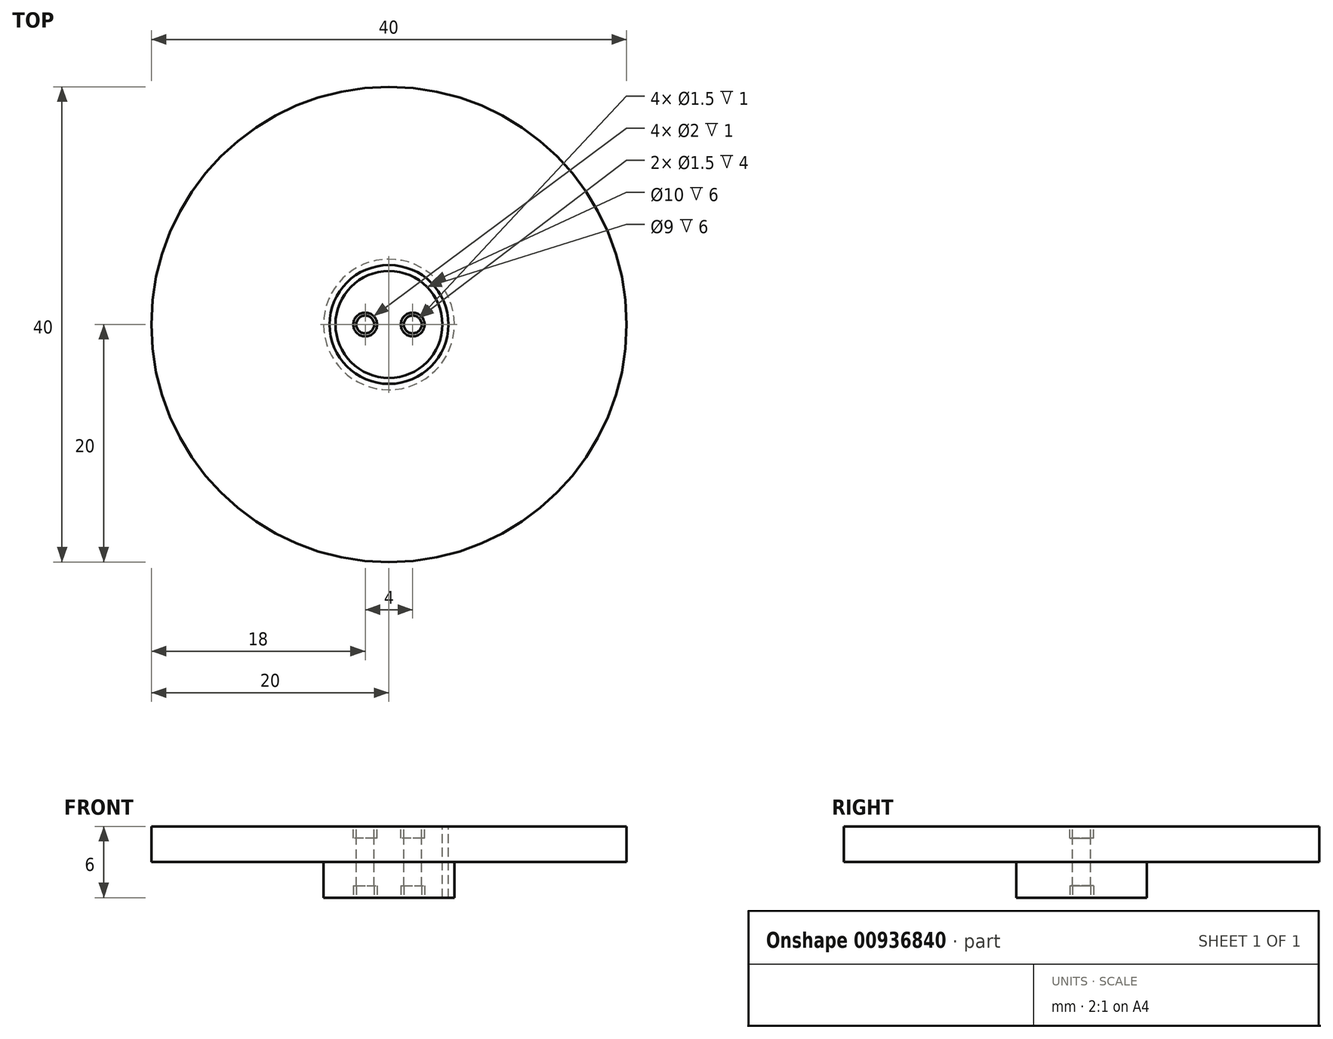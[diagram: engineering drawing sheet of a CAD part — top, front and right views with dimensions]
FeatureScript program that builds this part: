
annotation { "Feature Type Name" : "Feature", "Feature Type Description" : "" }
export const myFeature = defineFeature(function(context is Context, id is Id, definition is map)
    precondition{}
    {
        {
            var Q0;
            Q0=qCreatedBy(makeId("Top.planeOp"),FACE);
            var sketch = newSketch(context, id + "F0", { "sketchPlane" : qUnion([Q0])});
            skCircle(sketch, "E0", {"center": v(0, 0) * mm, "radius": 20 * mm});
            skCircle(sketch, "E1", {"center": v(0, 0) * mm, "radius": 5.5 * mm});
            skSolve(sketch);
        }
        {
            var Q0;
            Q0=makeQuery(id+"F0.imprint","IMPRINT",FACE,{"disambiguationData":[TD([[makeQuery(id+"F0.imprint","IMPRINT",EDGE,{"derivedFrom":sQuery(id+"F0.wireOp",EDGE,"E0")}),1.0]])]});
            extrude(context, id + "F1", {"entities" : qUnion([Q0]), "depth" : 3 * mm, "offsetDistance" : 25 * mm});
        }
        {
            var Q0;
            Q0=makeQuery(id+"F1.opExtrude","CAP_FACE",FACE,{"disambiguationData":[OSD([sQuery(id+"F0.wireOp",EDGE,"E0"),sQuery(id+"F0.wireOp",EDGE,"E1")])],"isStart":false});
            var sketch = newSketch(context, id + "F2", { "sketchPlane" : qUnion([Q0])});
            skCircle(sketch, "E2", {"center": v(0, 0) * mm, "radius": 5.5 * mm});
            skCircle(sketch, "E3", {"center": v(0, 0) * mm, "radius": 5 * mm});
            skSolve(sketch);
        }
        {
            var Q0;
            Q0 = qSketchRegion(id + "F2", true);
            extrude(context, id + "F3", {"entities" : qUnion([Q0]), "operationType" : NewBodyOperationType.ADD, "oppositeDirection" : true, "depth" : 6 * mm, "offsetDistance" : 25 * mm});
        }
        {
            var Q0;
            Q0=makeQuery(id+"F3.boolean.opBoolean","MERGE",FACE,{"derivedFrom":[makeQuery(id+"F1.opExtrude","CAP_FACE",FACE,{"disambiguationData":[OSD([sQuery(id+"F0.wireOp",EDGE,"E0"),sQuery(id+"F0.wireOp",EDGE,"E1")])],"isStart":false}),makeQuery(id+"F3.opExtrude","CAP_FACE",FACE,{"disambiguationData":[OSD([sQuery(id+"F2.wireOp",EDGE,"E2"),sQuery(id+"F2.wireOp",EDGE,"E3")])],"isStart":true})]});
            var sketch = newSketch(context, id + "F4", { "sketchPlane" : qUnion([Q0])});
            skCircle(sketch, "E4", {"center": v(0, 0) * mm, "radius": 5 * mm});
            skCircle(sketch, "E5", {"center": v(0, 0) * mm, "radius": 4.5 * mm});
            skSolve(sketch);
        }
        {
            var Q0;
            Q0 = qSketchRegion(id + "F4", true);
            extrude(context, id + "F5", {"entities" : qUnion([Q0]), "oppositeDirection" : true, "depth" : 6 * mm, "offsetDistance" : 25 * mm});
        }
        {
            var Q0;
            Q0=makeQuery(id+"F3.boolean.opBoolean","MERGE",FACE,{"derivedFrom":[makeQuery(id+"F1.opExtrude","CAP_FACE",FACE,{"disambiguationData":[OSD([sQuery(id+"F0.wireOp",EDGE,"E0"),sQuery(id+"F0.wireOp",EDGE,"E1")])],"isStart":false}),makeQuery(id+"F3.opExtrude","CAP_FACE",FACE,{"disambiguationData":[OSD([sQuery(id+"F2.wireOp",EDGE,"E2"),sQuery(id+"F2.wireOp",EDGE,"E3")])],"isStart":true})]});
            var sketch = newSketch(context, id + "F6", { "sketchPlane" : qUnion([Q0])});
            skCircle(sketch, "E6", {"center": v(0, 0) * mm, "radius": 4.5 * mm});
            skSolve(sketch);
        }
        {
            var Q0;
            Q0 = qSketchRegion(id + "F6", true);
            extrude(context, id + "F7", {"entities" : qUnion([Q0]), "oppositeDirection" : true, "depth" : 6 * mm, "offsetDistance" : 25 * mm});
        }
        {
            var Q0;
            Q0=makeQuery(id+"F3.boolean.opBoolean","MERGE",FACE,{"derivedFrom":[makeQuery(id+"F1.opExtrude","CAP_FACE",FACE,{"disambiguationData":[OSD([sQuery(id+"F0.wireOp",EDGE,"E0"),sQuery(id+"F0.wireOp",EDGE,"E1")])],"isStart":false}),makeQuery(id+"F3.opExtrude","CAP_FACE",FACE,{"disambiguationData":[OSD([sQuery(id+"F2.wireOp",EDGE,"E2"),sQuery(id+"F2.wireOp",EDGE,"E3")])],"isStart":true})]});
            var sketch = newSketch(context, id + "F8", { "sketchPlane" : qUnion([Q0])});
            skCircle(sketch, "E7", {"center": v(-2, 0) * mm, "radius": 1 * mm});
            skCircle(sketch, "E8", {"center": v(2, 0) * mm, "radius": 1 * mm});
            skSolve(sketch);
        }
        {
            var Q0;
            Q0 = qSketchRegion(id + "F8", true);
            extrude(context, id + "F9", {"entities" : qUnion([Q0]), "operationType" : NewBodyOperationType.REMOVE, "oppositeDirection" : true, "depth" : 1 * mm, "offsetDistance" : 25 * mm});
        }
        {
            var Q0;
            Q0=makeQuery(id+"F7.opExtrude","CAP_FACE",FACE,{"disambiguationData":[OSD([sQuery(id+"F6.wireOp",EDGE,"E6")])],"isStart":false});
            var sketch = newSketch(context, id + "F10", { "sketchPlane" : qUnion([Q0])});
            skCircle(sketch, "E9", {"center": v(-2, 0) * mm, "radius": 1 * mm});
            skCircle(sketch, "E10", {"center": v(2, 0) * mm, "radius": 1 * mm});
            skSolve(sketch);
        }
        {
            var Q0;
            Q0=makeQuery(id+"F7.opExtrude","CAP_FACE",FACE,{"disambiguationData":[OSD([sQuery(id+"F6.wireOp",EDGE,"E6")])],"isStart":true});
            var sketch = newSketch(context, id + "F11", { "sketchPlane" : qUnion([Q0])});
            skCircle(sketch, "E11", {"center": v(-2, 0) * mm, "radius": 1 * mm});
            skCircle(sketch, "E12", {"center": v(2, 0) * mm, "radius": 1 * mm});
            skCircle(sketch, "E13", {"center": v(-2, 0) * mm, "radius": 0.75 * mm});
            skCircle(sketch, "E14", {"center": v(2, 0) * mm, "radius": 0.75 * mm});
            skSolve(sketch);
        }
        {
            var Q0;
            Q0 = qSketchRegion(id + "F11", true);
            extrude(context, id + "F12", {"entities" : qUnion([Q0]), "oppositeDirection" : true, "depth" : 1 * mm, "offsetDistance" : 25 * mm});
        }
        {
            var Q0;
            Q0=makeQuery(id+"F7.opExtrude","CAP_FACE",FACE,{"disambiguationData":[OSD([sQuery(id+"F6.wireOp",EDGE,"E6")])],"isStart":true});
            var sketch = newSketch(context, id + "F13", { "sketchPlane" : qUnion([Q0])});
            skCircle(sketch, "E15", {"center": v(-2, 0) * mm, "radius": 0.75 * mm});
            skCircle(sketch, "E16", {"center": v(2, 0) * mm, "radius": 0.75 * mm});
            skSolve(sketch);
        }
        {
            var Q0;
            Q0 = qSketchRegion(id + "F13", true);
            extrude(context, id + "F14", {"entities" : qUnion([Q0]), "oppositeDirection" : true, "depth" : 9 * mm, "offsetDistance" : 25 * mm});
        }
        {
            var Q0;
            Q0=makeQuery(id+"F14.opExtrude","CAP_FACE",FACE,{"disambiguationData":[OSD([sQuery(id+"F13.wireOp",EDGE,"E15")])],"isStart":false});
            var sketch = newSketch(context, id + "F15", { "sketchPlane" : qUnion([Q0])});
            skArc(sketch, "E17", {"start": v(-1.28, 0.2) * mm, "mid": v(-2, 0.75) * mm, "end": v(-2.72, 0.2) * mm});
            skArc(sketch, "E18", {"start": v(2.72, 0.2) * mm, "mid": v(2, 0.75) * mm, "end": v(1.28, 0.2) * mm});
            skArc(sketch, "E19", {"start": v(-2.57, 0.2) * mm, "mid": v(-2, -0.6) * mm, "end": v(-1.43, 0.2) * mm});
            skArc(sketch, "E20", {"start": v(1.43, 0.2) * mm, "mid": v(2, -0.6) * mm, "end": v(2.57, 0.2) * mm});
            skLineSegment(sketch, "E21", {"start": v(-1.43, 0.2) * mm, "end": v(-1.28, 0.2) * mm});
            skLineSegment(sketch, "E22", {"start": v(-2.57, 0.2) * mm, "end": v(-2.72, 0.2) * mm});
            skLineSegment(sketch, "E23.trimOffspring", {"start": v(1.28, 0.2) * mm, "end": v(1.43, 0.2) * mm});
            skLineSegment(sketch, "E24.trimOffspring", {"start": v(2.57, 0.2) * mm, "end": v(2.72, 0.2) * mm});
            skSolve(sketch);
        }
        {
            var Q0;
            Q0 = qSketchRegion(id + "F15", true);
            extrude(context, id + "F16", {"entities" : qUnion([Q0]), "operationType" : NewBodyOperationType.REMOVE, "oppositeDirection" : true, "depth" : 3 * mm, "offsetDistance" : 25 * mm});
        }
        {
            var Q0;
            Q0=qCreatedBy(makeId("Right.planeOp"),FACE);
            var sketch = newSketch(context, id + "F17", { "sketchPlane" : qUnion([Q0])});
            skLineSegment(sketch, "E25.bottom", {"start": v(-6.18, -9) * mm, "end": v(0.2, -9) * mm});
            skLineSegment(sketch, "E25.top", {"start": v(-6.18, -10) * mm, "end": v(0.2, -10) * mm});
            skLineSegment(sketch, "E25.left", {"start": v(-6.18, -9) * mm, "end": v(-6.18, -10) * mm});
            skLineSegment(sketch, "E25.right", {"start": v(0.2, -9) * mm, "end": v(0.2, -10) * mm});
            skSolve(sketch);
        }
        {
            var Q0;
            Q0 = qSketchRegion(id + "F17", true);
            extrude(context, id + "F18", {"entities" : qUnion([Q0]), "operationType" : NewBodyOperationType.REMOVE, "endBound" : BoundingType.SYMMETRIC, "depth" : 25 * mm, "offsetDistance" : 25 * mm});
        }
        {
            var Q0;
            Q0=qCreatedBy(makeId("Right.planeOp"),FACE);
            var sketch = newSketch(context, id + "F19", { "sketchPlane" : qUnion([Q0])});
            skLineSegment(sketch, "E26.bottom", {"start": v(-1.5, -3.7) * mm, "end": v(0.3, -3.7) * mm});
            skLineSegment(sketch, "E26.top", {"start": v(-1.5, -3) * mm, "end": v(0.3, -3) * mm});
            skLineSegment(sketch, "E26.left", {"start": v(-1.5, -3.7) * mm, "end": v(-1.5, -3) * mm});
            skLineSegment(sketch, "E26.right", {"start": v(0.3, -3.7) * mm, "end": v(0.3, -3) * mm});
            skSolve(sketch);
        }
        {
            var Q0;
            Q0 = qSketchRegion(id + "F19", true);
            extrude(context, id + "F20", {"entities" : qUnion([Q0]), "operationType" : NewBodyOperationType.REMOVE, "endBound" : BoundingType.SYMMETRIC, "oppositeDirection" : true, "depth" : 25 * mm, "offsetDistance" : 25 * mm});
        }
        {
            var Q0;
            Q0 = qSketchRegion(id + "F10", true);
            extrude(context, id + "F21", {"entities" : qUnion([Q0]), "operationType" : NewBodyOperationType.REMOVE, "oppositeDirection" : true, "depth" : 1 * mm, "offsetDistance" : 25 * mm});
        }
        {
            var Q0;
            Q0=makeQuery(id+"F7.opExtrude","CAP_FACE",FACE,{"disambiguationData":[OSD([sQuery(id+"F6.wireOp",EDGE,"E6")])],"isStart":false});
            var sketch = newSketch(context, id + "F22", { "sketchPlane" : qUnion([Q0])});
            skCircle(sketch, "E27", {"center": v(-2, 0) * mm, "radius": 1 * mm});
            skCircle(sketch, "E28", {"center": v(-2, 0) * mm, "radius": 0.75 * mm});
            skCircle(sketch, "E29", {"center": v(2, 0) * mm, "radius": 1 * mm});
            skCircle(sketch, "E30", {"center": v(2, 0) * mm, "radius": 0.75 * mm});
            skSolve(sketch);
        }
        {
            var Q0;
            Q0 = qSketchRegion(id + "F22", true);
            extrude(context, id + "F23", {"entities" : qUnion([Q0]), "oppositeDirection" : true, "depth" : 1 * mm, "offsetDistance" : 25 * mm});
        }
        {
            var Q0;
            Q0=makeQuery(id+"F9.boolean.opBoolean","COPY",FACE,{"derivedFrom":makeQuery(id+"F9.opExtrude","CAP_FACE",FACE,{"disambiguationData":[OSD([sQuery(id+"F8.wireOp",EDGE,"E8")])],"isStart":false})});
            var sketch = newSketch(context, id + "F24", { "sketchPlane" : qUnion([Q0])});
            skCircle(sketch, "E31", {"center": v(-2, 0) * mm, "radius": 0.75 * mm});
            skCircle(sketch, "E32", {"center": v(2, 0) * mm, "radius": 0.75 * mm});
            skSolve(sketch);
        }
        {
            var Q0;
            Q0 = qSketchRegion(id + "F24", true);
            extrude(context, id + "F25", {"entities" : qUnion([Q0]), "operationType" : NewBodyOperationType.REMOVE, "oppositeDirection" : true, "depth" : 25 * mm, "offsetDistance" : 25 * mm});
        }
    });
